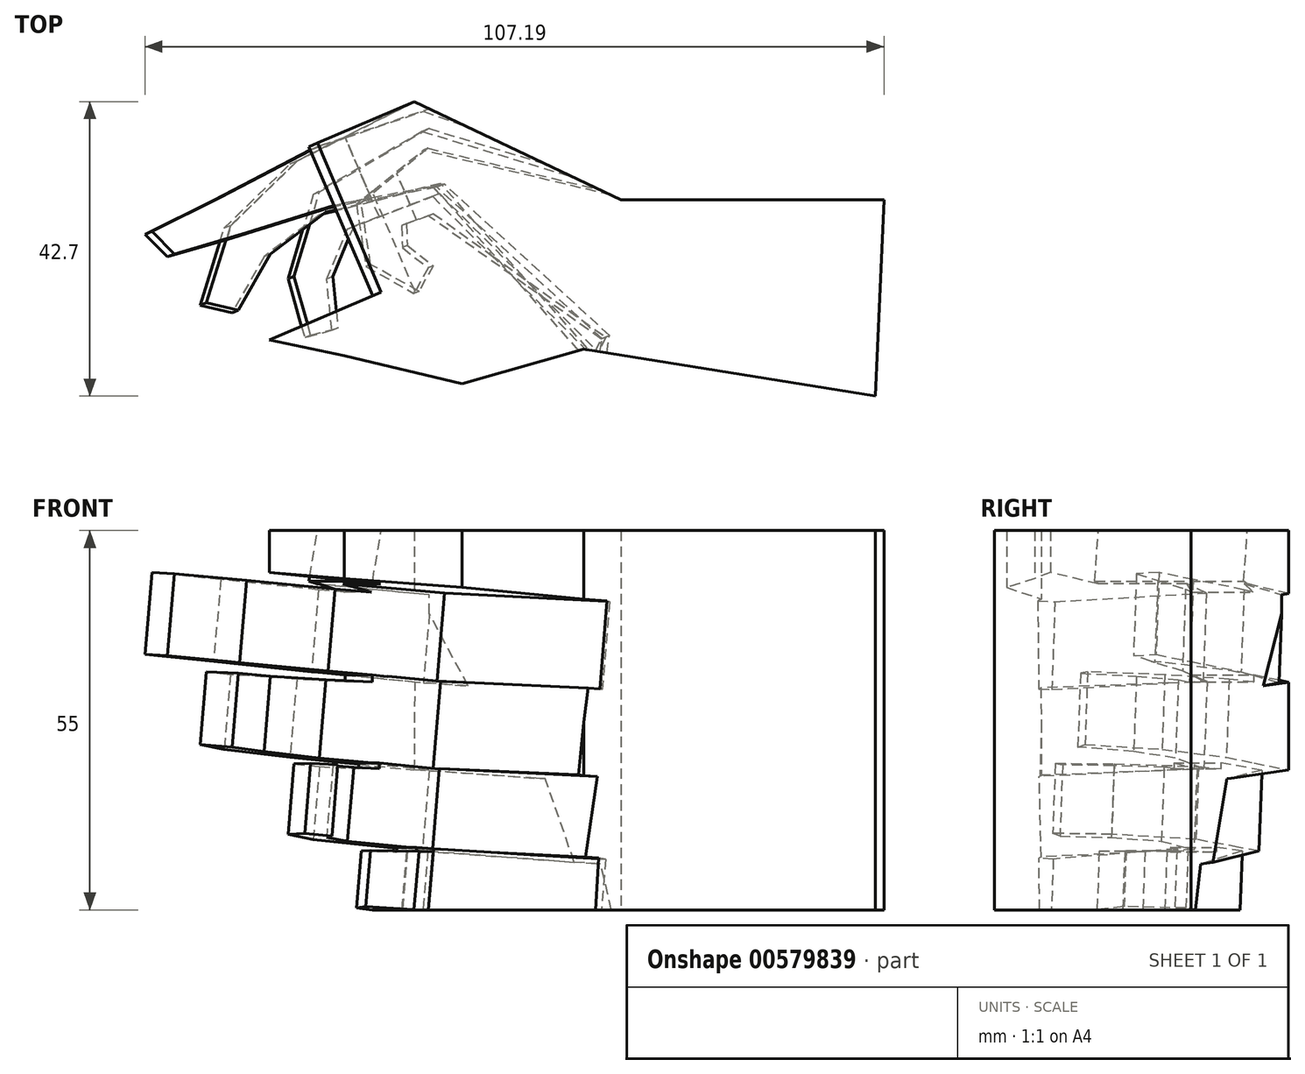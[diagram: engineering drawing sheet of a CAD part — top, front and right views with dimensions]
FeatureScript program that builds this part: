
annotation { "Feature Type Name" : "Feature", "Feature Type Description" : "" }
export const myFeature = defineFeature(function(context is Context, id is Id, definition is map)
    precondition{}
    {
        {
            var Q0;
            Q0=qCreatedBy(makeId("Top.planeOp"),FACE);
            var sketch = newSketch(context, id + "F0", { "sketchPlane" : qUnion([Q0])});
            skLineSegment(sketch, "E0", {"start": v(-33.79, -15.38) * mm, "end": v(6.43, 1.78) * mm});
            skLineSegment(sketch, "E1", {"start": v(6.43, 1.78) * mm, "end": v(36.38, -12.43) * mm});
            skLineSegment(sketch, "E2", {"start": v(36.38, -12.43) * mm, "end": v(74.52, -12.43) * mm});
            skLineSegment(sketch, "E3", {"start": v(74.52, -12.43) * mm, "end": v(73.23, -40.92) * mm});
            skLineSegment(sketch, "E4", {"start": v(73.23, -40.92) * mm, "end": v(30.95, -34.09) * mm});
            skLineSegment(sketch, "E5", {"start": v(30.95, -34.09) * mm, "end": v(13.3, -39.13) * mm});
            skLineSegment(sketch, "E6", {"start": v(13.3, -39.13) * mm, "end": v(-3.78, -35.04) * mm});
            skLineSegment(sketch, "E7", {"start": v(-3.78, -35.04) * mm, "end": v(-25.7, -30.45) * mm});
            skLineSegment(sketch, "E8", {"start": v(-25.7, -30.45) * mm, "end": v(-33.79, -15.38) * mm});
            skSolve(sketch);
        }
        {
            var Q0;
            Q0 = qSketchRegion(id + "F0", true);
            extrude(context, id + "F1", {"entities" : qUnion([Q0]), "depth" : 55 * mm, "offsetDistance" : 25 * mm});
        }
        {
            var Q0;
            Q0=makeQuery(id+"F1.opExtrude","SWEPT_FACE",FACE,{"disambiguationData":[OSD([sQuery(id+"F0.wireOp",EDGE,"E0")])]});
            var sketch = newSketch(context, id + "F2", { "sketchPlane" : qUnion([Q0])});
            skPoint(sketch, "E9.0", {"position": v(37.11, 55) * mm});
            skPoint(sketch, "E9.1", {"position": v(37.11, 0) * mm});
            skLineSegment(sketch, "E10", {"start": v(37.11, 55) * mm, "end": v(37.11, 0) * mm});
            skLineSegment(sketch, "E11", {"start": v(37.11, 3.04) * mm, "end": v(4.13, 0) * mm});
            skLineSegment(sketch, "E12", {"start": v(37.11, 0) * mm, "end": v(4.13, 0) * mm});
            skLineSegment(sketch, "E13", {"start": v(37.11, 9.32) * mm, "end": v(-0.17, 8.4) * mm});
            skLineSegment(sketch, "E14", {"start": v(-0.17, 8.4) * mm, "end": v(-0.17, 9.08) * mm});
            skLineSegment(sketch, "E15", {"start": v(-0.17, 9.08) * mm, "end": v(37.11, 12.52) * mm});
            skLineSegment(sketch, "E16", {"start": v(37.11, 22.03) * mm, "end": v(4.66, 20.47) * mm});
            skLineSegment(sketch, "E17", {"start": v(4.66, 20.47) * mm, "end": v(4.66, 21.31) * mm});
            skLineSegment(sketch, "E18", {"start": v(4.66, 21.31) * mm, "end": v(37.11, 24.3) * mm});
            skLineSegment(sketch, "E19", {"start": v(37.11, 34.75) * mm, "end": v(4.66, 33.03) * mm});
            skLineSegment(sketch, "E20", {"start": v(4.66, 33.03) * mm, "end": v(4.66, 34.06) * mm});
            skLineSegment(sketch, "E21", {"start": v(4.66, 34.06) * mm, "end": v(37.11, 37.05) * mm});
            skLineSegment(sketch, "E22", {"start": v(37.11, 49.04) * mm, "end": v(4.66, 46.05) * mm});
            skLineSegment(sketch, "E23", {"start": v(4.66, 46.05) * mm, "end": v(10.05, 47.68) * mm});
            skLineSegment(sketch, "E24", {"start": v(10.05, 47.68) * mm, "end": v(8.68, 55) * mm});
            skLineSegment(sketch, "E25", {"start": v(37.11, 55) * mm, "end": v(8.68, 55) * mm});
            skSolve(sketch);
        }
        {
            var Q0;
            {var subQ0=sQuery(id+"F2.wireOp",EDGE,"E12");var subQ1=sQuery(id+"F2.wireOp",EDGE,"E10");var subQ2=makeQuery(id+"F2.imprint","INTERSECT",VERTEX,{"derivedFrom":[subQ1,subQ0]});Q0=makeQuery(id+"F2.imprint","IMPRINT",FACE,{"disambiguationData":[TD([[makeQuery(id+"F2.imprint","IMPRINT",EDGE,{"disambiguationData":[TD([[subQ2,1.0]])],"derivedFrom":subQ1}),-1.0]])]});}
            var Q1;
            {var subQ0=sQuery(id+"F2.wireOp",EDGE,"E13");var subQ1=sQuery(id+"F2.wireOp",EDGE,"E10");var subQ2=makeQuery(id+"F2.imprint","INTERSECT",VERTEX,{"derivedFrom":[subQ1,subQ0]});Q1=makeQuery(id+"F2.imprint","IMPRINT",FACE,{"disambiguationData":[TD([[makeQuery(id+"F2.imprint","IMPRINT",EDGE,{"disambiguationData":[TD([[subQ2,1.0]])],"derivedFrom":subQ1}),-1.0]])]});}
            var Q2;
            {var subQ0=sQuery(id+"F2.wireOp",EDGE,"E16");var subQ1=sQuery(id+"F2.wireOp",EDGE,"E10");var subQ2=makeQuery(id+"F2.imprint","INTERSECT",VERTEX,{"derivedFrom":[subQ1,subQ0]});Q2=makeQuery(id+"F2.imprint","IMPRINT",FACE,{"disambiguationData":[TD([[makeQuery(id+"F2.imprint","IMPRINT",EDGE,{"disambiguationData":[TD([[subQ2,1.0]])],"derivedFrom":subQ1}),-1.0]])]});}
            var Q3;
            {var subQ0=sQuery(id+"F2.wireOp",EDGE,"E19");var subQ1=sQuery(id+"F2.wireOp",EDGE,"E10");var subQ2=makeQuery(id+"F2.imprint","INTERSECT",VERTEX,{"derivedFrom":[subQ1,subQ0]});Q3=makeQuery(id+"F2.imprint","IMPRINT",FACE,{"disambiguationData":[TD([[makeQuery(id+"F2.imprint","IMPRINT",EDGE,{"disambiguationData":[TD([[subQ2,1.0]])],"derivedFrom":subQ1}),-1.0]])]});}
            var Q4;
            {var subQ0=sQuery(id+"F2.wireOp",EDGE,"E20");Q4=makeQuery(id+"F2.imprint","IMPRINT",FACE,{"disambiguationData":[TD([[makeQuery(id+"F2.imprint","IMPRINT",EDGE,{"derivedFrom":subQ0}),-1.0]])]});}
            var Q5;
            {var subQ0=sQuery(id+"F2.wireOp",EDGE,"E17");Q5=makeQuery(id+"F2.imprint","IMPRINT",FACE,{"disambiguationData":[TD([[makeQuery(id+"F2.imprint","IMPRINT",EDGE,{"derivedFrom":subQ0}),-1.0]])]});}
            var Q6;
            {var subQ0=sQuery(id+"F2.wireOp",EDGE,"E14");Q6=makeQuery(id+"F2.imprint","IMPRINT",FACE,{"disambiguationData":[TD([[makeQuery(id+"F2.imprint","IMPRINT",EDGE,{"derivedFrom":subQ0}),-1.0]])]});}
            var Q7;
            {var subQ0=sQuery(id+"F2.wireOp",EDGE,"E12");var subQ1=sQuery(id+"F2.wireOp",EDGE,"E11");var subQ2=sQuery(id+"F0.wireOp",EDGE,"E0");var subQ3=makeQuery(id+"F2.imprint","INTERSECT",VERTEX,{"derivedFrom":[makeQuery(id+"F1.opExtrude","CAP_EDGE",EDGE,{"disambiguationData":[OSD([subQ2])],"isStart":true}),subQ1,subQ0]});Q7=makeQuery(id+"F2.imprint","IMPRINT",FACE,{"disambiguationData":[TD([[makeQuery(id+"F2.imprint","IMPRINT",EDGE,{"disambiguationData":[TD([[subQ3,1.0]])],"derivedFrom":subQ1}),1.0]])]});}
            extrude(context, id + "F3", {"entities" : qUnion([Q0, Q1, Q2, Q3, Q4, Q5, Q6, Q7]), "operationType" : NewBodyOperationType.REMOVE, "oppositeDirection" : true, "depth" : 155.8 * mm, "offsetDistance" : 25 * mm, "symmetric" : true});
        }
        {
            var Q0;
            {var subQ0=sQuery(id+"F2.wireOp",EDGE,"E25");var subQ1=sQuery(id+"F2.wireOp",EDGE,"E10");var subQ2=makeQuery(id+"F2.imprint","INTERSECT",VERTEX,{"derivedFrom":[subQ1,subQ0]});Q0=makeQuery(id+"F2.imprint","IMPRINT",FACE,{"disambiguationData":[TD([[makeQuery(id+"F2.imprint","IMPRINT",EDGE,{"disambiguationData":[TD([[subQ2,-1.0]])],"derivedFrom":subQ1}),-1.0]])]});}
            var Q1;
            {var subQ5=sQuery(id+"F2.wireOp",EDGE,"E23");Q1=makeQuery(id+"F2.imprint","IMPRINT",FACE,{"disambiguationData":[TD([[makeQuery(id+"F2.imprint","IMPRINT",EDGE,{"derivedFrom":subQ5}),-1.0]])]});}
            extrude(context, id + "F4", {"entities" : qUnion([Q0, Q1]), "operationType" : NewBodyOperationType.REMOVE, "oppositeDirection" : true, "depth" : 23.5 * mm, "offsetDistance" : 25 * mm});
        }
        {
            var Q0;
            Q0=makeQuery(id+"F3.boolean.opBoolean","COPY",FACE,{"derivedFrom":makeQuery(id+"F3.opExtrude","SWEPT_FACE",FACE,{"disambiguationData":[OSD([sQuery(id+"F2.wireOp",EDGE,"E11")])]})});
            var sketch = newSketch(context, id + "F5", { "sketchPlane" : qUnion([Q0])});
            skLineSegment(sketch, "E26.0", {"start": v(7.64, 5.27) * mm, "end": v(36.11, 12.05) * mm});
            skLineSegment(sketch, "E27", {"start": v(7.64, 5.27) * mm, "end": v(-1.98, 13.13) * mm});
            skLineSegment(sketch, "E28", {"start": v(-1.98, 13.13) * mm, "end": v(-0.6, 22.12) * mm});
            skLineSegment(sketch, "E29", {"start": v(4.7, 19.38) * mm, "end": v(4.57, 16.2) * mm});
            skLineSegment(sketch, "E30", {"start": v(4.57, 16.2) * mm, "end": v(8.46, 14.77) * mm});
            skLineSegment(sketch, "E31", {"start": v(8.46, 14.77) * mm, "end": v(22.51, 24.78) * mm});
            skLineSegment(sketch, "E32", {"start": v(22.51, 24.78) * mm, "end": v(33.5, 32.62) * mm});
            skLineSegment(sketch, "E33", {"start": v(33.5, 32.62) * mm, "end": v(8.02, 84.52) * mm});
            skLineSegment(sketch, "E34", {"start": v(8.02, 84.52) * mm, "end": v(-41.3, 11.1) * mm});
            skLineSegment(sketch, "E35", {"start": v(-41.3, 11.1) * mm, "end": v(12.8, -16.94) * mm});
            skLineSegment(sketch, "E36", {"start": v(12.8, -16.94) * mm, "end": v(36.11, 12.05) * mm});
            skLineSegment(sketch, "E37", {"start": v(-0.6, 22.12) * mm, "end": v(6.4, 26) * mm});
            skLineSegment(sketch, "E38", {"start": v(6.4, 26) * mm, "end": v(8.45, 22.3) * mm});
            skLineSegment(sketch, "E39", {"start": v(8.45, 22.3) * mm, "end": v(4.7, 19.38) * mm});
            skSolve(sketch);
        }
        {
            var Q0;
            Q0 = qSketchRegion(id + "F5", true);
            extrude(context, id + "F6", {"entities" : qUnion([Q0]), "operationType" : NewBodyOperationType.REMOVE, "oppositeDirection" : true, "depth" : 9.43 * mm, "offsetDistance" : 25 * mm});
        }
        {
            var Q0;
            Q0=makeQuery(id+"F3.boolean.opBoolean","COPY",FACE,{"derivedFrom":makeQuery(id+"F3.opExtrude","SWEPT_FACE",FACE,{"disambiguationData":[OSD([sQuery(id+"F2.wireOp",EDGE,"E15")])]})});
            var sketch = newSketch(context, id + "F7", { "sketchPlane" : qUnion([Q0])});
            skPoint(sketch, "E40.0", {"position": v(6.8, 2.85) * mm});
            skLineSegment(sketch, "E41", {"start": v(6.8, 2.85) * mm, "end": v(-9.04, 12.04) * mm});
            skLineSegment(sketch, "E42", {"start": v(-9.04, 12.04) * mm, "end": v(-12.72, 24.28) * mm});
            skLineSegment(sketch, "E43", {"start": v(-12.72, 24.28) * mm, "end": v(-10.3, 32.83) * mm});
            skLineSegment(sketch, "E44", {"start": v(-6.35, 31.77) * mm, "end": v(-10.3, 32.83) * mm});
            skLineSegment(sketch, "E45", {"start": v(8.3, 12.27) * mm, "end": v(32.96, 36.75) * mm});
            skLineSegment(sketch, "E46", {"start": v(32.96, 36.75) * mm, "end": v(32.96, 95.86) * mm});
            skLineSegment(sketch, "E47", {"start": v(32.96, 95.86) * mm, "end": v(-56.5, 43.07) * mm});
            skLineSegment(sketch, "E48", {"start": v(-56.5, 43.07) * mm, "end": v(-55.7, -33.7) * mm});
            skLineSegment(sketch, "E49", {"start": v(-55.7, -33.7) * mm, "end": v(14.54, -54.3) * mm});
            skLineSegment(sketch, "E50", {"start": v(6.8, 2.85) * mm, "end": v(33, 10.66) * mm});
            skLineSegment(sketch, "E51", {"start": v(33, 10.66) * mm, "end": v(14.54, -54.3) * mm});
            skLineSegment(sketch, "E52", {"start": v(-6.35, 31.77) * mm, "end": v(-7.12, 24.31) * mm});
            skLineSegment(sketch, "E53", {"start": v(-7.12, 24.31) * mm, "end": v(-4.08, 17.04) * mm});
            skLineSegment(sketch, "E54", {"start": v(-4.08, 17.04) * mm, "end": v(8.3, 12.27) * mm});
            skSolve(sketch);
        }
        {
            var Q0;
            Q0 = qSketchRegion(id + "F7", true);
            extrude(context, id + "F8", {"entities" : qUnion([Q0]), "operationType" : NewBodyOperationType.REMOVE, "oppositeDirection" : true, "depth" : 11.75 * mm, "offsetDistance" : 25 * mm});
        }
        {
            var Q0;
            Q0=makeQuery(id+"F3.boolean.opBoolean","COPY",FACE,{"derivedFrom":makeQuery(id+"F3.opExtrude","SWEPT_FACE",FACE,{"disambiguationData":[OSD([sQuery(id+"F2.wireOp",EDGE,"E18")])]})});
            var sketch = newSketch(context, id + "F9", { "sketchPlane" : qUnion([Q0])});
            skPoint(sketch, "E55.0", {"position": v(4.69, -1.05) * mm});
            skLineSegment(sketch, "E56", {"start": v(4.69, -1.05) * mm, "end": v(22.38, 7.26) * mm});
            skLineSegment(sketch, "E57", {"start": v(22.38, 7.26) * mm, "end": v(35.36, -12.13) * mm});
            skLineSegment(sketch, "E58", {"start": v(35.36, -12.13) * mm, "end": v(-58.96, -29.6) * mm});
            skLineSegment(sketch, "E59", {"start": v(-58.96, -29.6) * mm, "end": v(-77.94, 38.16) * mm});
            skLineSegment(sketch, "E60", {"start": v(-77.94, 38.16) * mm, "end": v(25.27, 80.38) * mm});
            skLineSegment(sketch, "E61", {"start": v(25.27, 80.38) * mm, "end": v(34.1, 41.17) * mm});
            skLineSegment(sketch, "E62", {"start": v(34.1, 41.17) * mm, "end": v(7.4, 11.27) * mm});
            skLineSegment(sketch, "E63", {"start": v(7.4, 11.27) * mm, "end": v(-9.17, 15.44) * mm});
            skLineSegment(sketch, "E64", {"start": v(-9.17, 15.44) * mm, "end": v(-17.23, 21.52) * mm});
            skLineSegment(sketch, "E65", {"start": v(-17.23, 21.52) * mm, "end": v(-21.88, 29.65) * mm});
            skLineSegment(sketch, "E66", {"start": v(-21.88, 29.65) * mm, "end": v(-26.52, 28.62) * mm});
            skLineSegment(sketch, "E67", {"start": v(-26.52, 28.62) * mm, "end": v(-23.04, 17.42) * mm});
            skLineSegment(sketch, "E68", {"start": v(-23.04, 17.42) * mm, "end": v(-13.42, 8.05) * mm});
            skLineSegment(sketch, "E69", {"start": v(-13.42, 8.05) * mm, "end": v(4.69, -1.05) * mm});
            skSolve(sketch);
        }
        {
            var Q0;
            Q0 = qSketchRegion(id + "F9", true);
            extrude(context, id + "F10", {"entities" : qUnion([Q0]), "operationType" : NewBodyOperationType.REMOVE, "oppositeDirection" : true, "depth" : 12.7 * mm, "offsetDistance" : 25 * mm});
        }
        {
            var Q0;
            Q0=makeQuery(id+"F3.boolean.opBoolean","COPY",FACE,{"derivedFrom":makeQuery(id+"F3.opExtrude","SWEPT_FACE",FACE,{"disambiguationData":[OSD([sQuery(id+"F2.wireOp",EDGE,"E21")])]})});
            var sketch = newSketch(context, id + "F11", { "sketchPlane" : qUnion([Q0])});
            skLineSegment(sketch, "E70", {"start": v(4.93, 0.8) * mm, "end": v(26.43, 8.36) * mm});
            skLineSegment(sketch, "E71", {"start": v(26.43, 8.36) * mm, "end": v(70.46, -55.46) * mm});
            skLineSegment(sketch, "E72", {"start": v(70.46, -55.46) * mm, "end": v(-55.99, -63.57) * mm});
            skLineSegment(sketch, "E73", {"start": v(-55.99, -63.57) * mm, "end": v(-70.56, 39.9) * mm});
            skLineSegment(sketch, "E74", {"start": v(-70.56, 39.9) * mm, "end": v(17.08, 125.23) * mm});
            skLineSegment(sketch, "E75", {"start": v(17.08, 125.23) * mm, "end": v(30.9, 33.72) * mm});
            skLineSegment(sketch, "E76", {"start": v(30.9, 33.72) * mm, "end": v(6.88, 11.83) * mm});
            skLineSegment(sketch, "E77", {"start": v(6.88, 11.83) * mm, "end": v(-8.97, 14.87) * mm});
            skLineSegment(sketch, "E78", {"start": v(-8.97, 14.87) * mm, "end": v(-21.83, 18.95) * mm});
            skLineSegment(sketch, "E79", {"start": v(-21.83, 18.95) * mm, "end": v(-32.34, 22.05) * mm});
            skLineSegment(sketch, "E80", {"start": v(-32.34, 22.05) * mm, "end": v(-35.63, 18.8) * mm});
            skLineSegment(sketch, "E81", {"start": v(-35.63, 18.8) * mm, "end": v(-25.62, 13.78) * mm});
            skLineSegment(sketch, "E82", {"start": v(-25.62, 13.78) * mm, "end": v(-11.38, 6.37) * mm});
            skLineSegment(sketch, "E83", {"start": v(-11.38, 6.37) * mm, "end": v(4.93, 0.8) * mm});
            skSolve(sketch);
        }
        {
            var Q0;
            Q0 = qSketchRegion(id + "F11", true);
            extrude(context, id + "F12", {"entities" : qUnion([Q0]), "operationType" : NewBodyOperationType.REMOVE, "oppositeDirection" : true, "depth" : 12.8 * mm, "offsetDistance" : 25 * mm});
        }
    });
